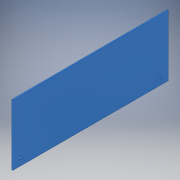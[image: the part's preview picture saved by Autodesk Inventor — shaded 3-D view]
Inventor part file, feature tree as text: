
AUTODESK INVENTOR PART (.ipt)
format: ipt  version: 2017 (Build 210142000, 142)  size: 121,856 bytes
history: native  units: in
note: dims shown in document units (in); Inventor stores cm internally (conversion verified against a paired STEP export)
features: extrude x5, sketch x5
ambient origin geometry x8: Origin, YZ Plane, XZ Plane, XY Plane, X Axis, Y Axis, Z Axis, Center Point
bodies: Solid1 (feature_tree)
feature tree (10):
  extrude  "Extrusion1"  Depth=20.0in
  extrude  "Extrusion2"  Depth=0.125in
  extrude  "Extrusion3"  Depth=0.1562in
  extrude  "Extrusion4"  Depth=1.0in
  extrude  "Extrusion5"  Depth=0.125in TaperAngle=0.0deg
  sketch  "Sketch1"  dims[d0=7.875in d1=20.0in]
  sketch  "Sketch3"  dims[d2=0.125in d3=0.0in d8=0.875in]
  sketch  "Sketch4"  dims[d9=1.0in d10=0.1562in]
  sketch  "Sketch5"  dims[d11=0.875in d12=1.0in]
  sketch  "Sketch6"  dims[d13=0.1562in d14=0.125in d15=0.0in d16=0.875in d17=1.0in d18=0.1562in d19=0.125in d20=0.0in d21=0.3125in d22=0.125in d23=0.0in d24=0.3125in d25=0.125in d26=0.0in]
